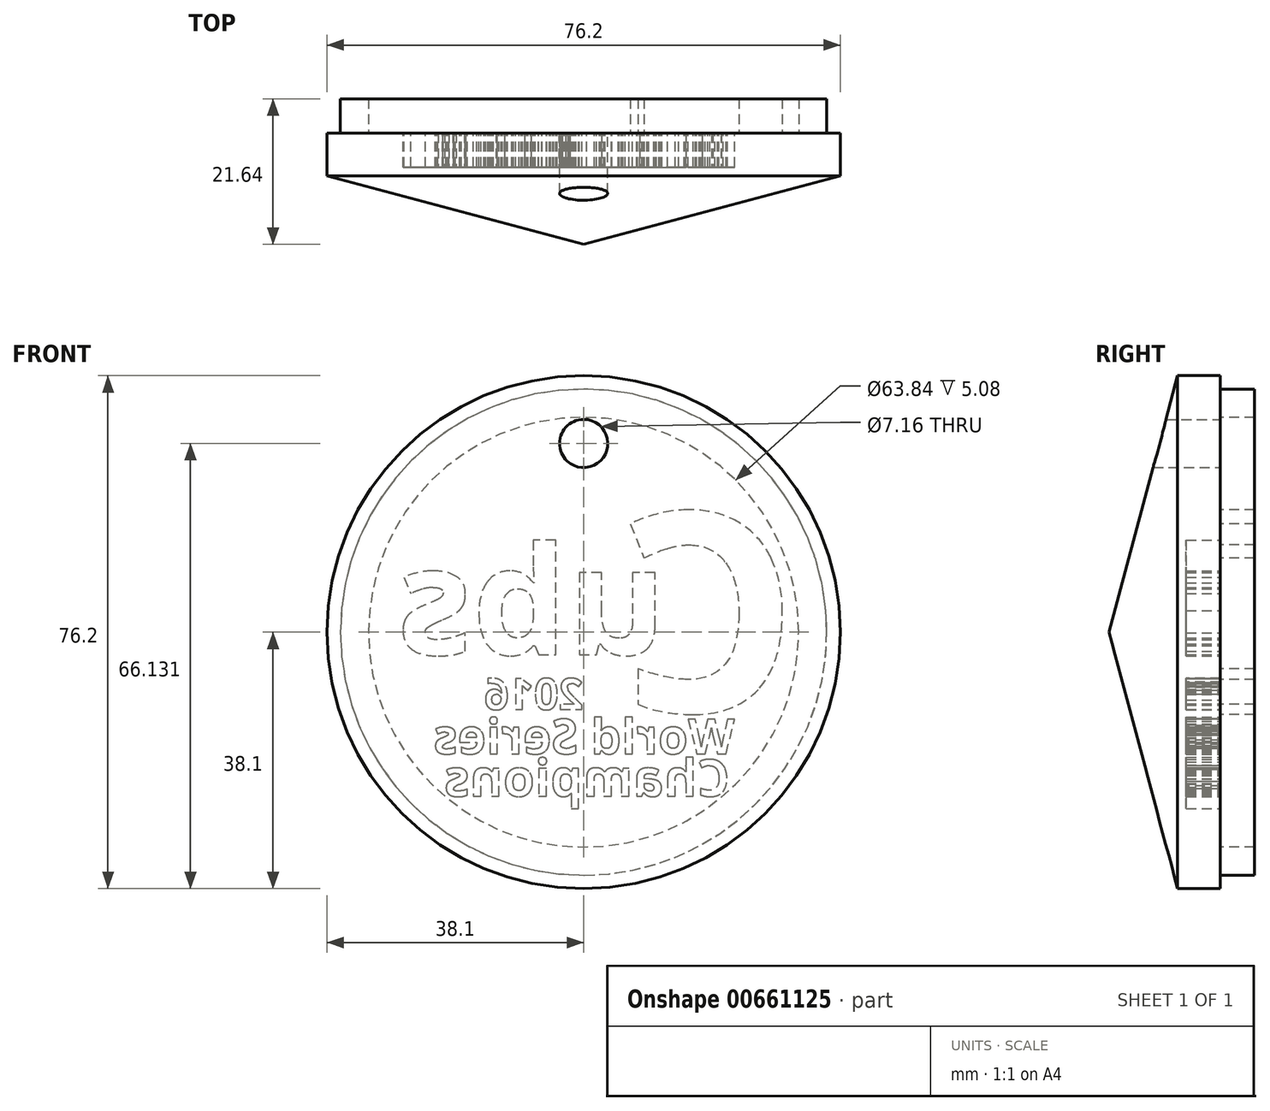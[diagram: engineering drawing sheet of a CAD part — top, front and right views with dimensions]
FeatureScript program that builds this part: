
annotation { "Feature Type Name" : "Feature", "Feature Type Description" : "" }
export const myFeature = defineFeature(function(context is Context, id is Id, definition is map)
    precondition{}
    {
        {
            var Q0;
            Q0=qCreatedBy(makeId("Front.planeOp"),FACE);
            var sketch = newSketch(context, id + "F0", { "sketchPlane" : qUnion([Q0])});
            skCircle(sketch, "E0", {"center": v(0, 0) * mm, "radius": 38.1 * mm});
            skSolve(sketch);
        }
        {
            var Q0;
            Q0=makeQuery(id+"F0.imprint","IMPRINT",FACE,{"disambiguationData":[TD([[makeQuery(id+"F0.imprint","IMPRINT",EDGE,{"derivedFrom":sQuery(id+"F0.wireOp",EDGE,"E0")}),1.0]])]});
            extrude(context, id + "F1", {"entities" : qUnion([Q0]), "oppositeDirection" : true, "depth" : 6.35 * mm, "offsetDistance" : 25.4 * mm});
        }
        {
            var Q0;
            Q0=makeQuery(id+"F1.opExtrude","CAP_FACE",FACE,{"disambiguationData":[OSD([sQuery(id+"F0.wireOp",EDGE,"E0")])],"isStart":false});
            var sketch = newSketch(context, id + "F2", { "sketchPlane" : qUnion([Q0])});
            skText(sketch, "E1", { "text": "C", "fontName": "OpenSans-Bold.ttf"});
            const initialGuessF2  = {"E1": [-0.0319, -0.01183, 1, 0, 0.02984]};
            skSetInitialGuess(sketch, initialGuessF2);
            skSolve(sketch);
        }
        {
            var Q0;
            Q0=makeQuery(id+"F2.imprint","IMPRINT",FACE,{"disambiguationData":[TD([[makeQuery(id+"F2.imprint","IMPRINT",EDGE,{"derivedFrom":sQuery(id+"F2.wireOp",EDGE,"E1.sketch_text.stroke-0")}),1.0]])]});
            var sketch = newSketch(context, id + "F3", { "sketchPlane" : qUnion([Q0])});
            skText(sketch, "E2", { "text": "ubs", "fontName": "OpenSans-Bold.ttf"});
            const initialGuessF3  = {"E2": [-0.01228, -0.00332, 1, 0, 0.01609]};
            skSetInitialGuess(sketch, initialGuessF3);
            skSolve(sketch);
        }
        {
            var Q0;
            Q0=makeQuery(id+"F3.imprint","IMPRINT",FACE,{"disambiguationData":[TD([[makeQuery(id+"F3.imprint","IMPRINT",EDGE,{"derivedFrom":sQuery(id+"F3.wireOp",EDGE,"E2.sketch_text.stroke-0")}),-1.0]])]});
            var Q1;
            Q1=makeQuery(id+"F3.imprint","IMPRINT",FACE,{"disambiguationData":[TD([[makeQuery(id+"F3.imprint","IMPRINT",EDGE,{"derivedFrom":sQuery(id+"F3.wireOp",EDGE,"E2.sketch_text.stroke-40")}),-1.0]])]});
            var Q2;
            Q2=makeQuery(id+"F3.imprint","IMPRINT",FACE,{"disambiguationData":[TD([[makeQuery(id+"F3.imprint","IMPRINT",EDGE,{"derivedFrom":sQuery(id+"F3.wireOp",EDGE,"E2.sketch_text.stroke-17")}),-1.0]])]});
            var Q3;
            Q3=makeQuery(id+"F1.opExtrude","CAP_FACE",FACE,{"disambiguationData":[OSD([sQuery(id+"F0.wireOp",EDGE,"E0")])],"isStart":true});
            extrude(context, id + "F4", {"entities" : qUnion([Q0, Q1, Q2, Q3]), "operationType" : NewBodyOperationType.REMOVE, "oppositeDirection" : true, "depth" : 5.08 * mm, "offsetDistance" : 25.4 * mm});
        }
        {
            var Q0;
            Q0=makeQuery(id+"F1.opExtrude","CAP_FACE",FACE,{"disambiguationData":[OSD([sQuery(id+"F0.wireOp",EDGE,"E0")])],"isStart":true});
            extrude(context, id + "F5", {"entities" : qUnion([Q0]), "operationType" : NewBodyOperationType.ADD, "depth" : 25.4 * mm, "offsetDistance" : 25.4 * mm, "hasDraft" : true, "draftAngle" : 75 * degree, "draftPullDirection" : true});
        }
        {
            var Q0;
            {var subQ0=sQuery(id+"F0.wireOp",EDGE,"E0");Q0=makeQuery(id+"F4.boolean.opBoolean","SPLIT",FACE,{"disambiguationData":[TD([makeQuery(id+"F1.opExtrude","SWEPT_FACE",FACE,{"disambiguationData":[OSD([subQ0])]})])],"derivedFrom":makeQuery(id+"F1.opExtrude","CAP_FACE",FACE,{"disambiguationData":[OSD([subQ0])],"isStart":false})});}
            var sketch = newSketch(context, id + "F6", { "sketchPlane" : qUnion([Q0])});
            skCircle(sketch, "E3", {"center": v(0, 28.03) * mm, "radius": 3.58 * mm});
            skSolve(sketch);
        }
        {
            var Q0;
            Q0=makeQuery(id+"F6.imprint","IMPRINT",FACE,{"disambiguationData":[TD([[makeQuery(id+"F6.imprint","IMPRINT",EDGE,{"derivedFrom":sQuery(id+"F6.wireOp",EDGE,"E3")}),1.0]])]});
            extrude(context, id + "F7", {"entities" : qUnion([Q0]), "operationType" : NewBodyOperationType.REMOVE, "oppositeDirection" : true, "depth" : 25.4 * mm, "offsetDistance" : 25.4 * mm});
        }
        {
            var Q0;
            Q0=makeQuery(id+"F4.boolean.opBoolean","COPY",FACE,{"derivedFrom":makeQuery(id+"F4.opExtrude","CAP_FACE",FACE,{"disambiguationData":[OSD([sQuery(id+"F3.wireOp",EDGE,"E2.sketch_text.stroke-0"),sQuery(id+"F3.wireOp",EDGE,"E2.sketch_text.stroke-1"),sQuery(id+"F3.wireOp",EDGE,"E2.sketch_text.stroke-2"),sQuery(id+"F3.wireOp",EDGE,"E2.sketch_text.stroke-3"),sQuery(id+"F3.wireOp",EDGE,"E2.sketch_text.stroke-4"),sQuery(id+"F3.wireOp",EDGE,"E2.sketch_text.stroke-5"),sQuery(id+"F3.wireOp",EDGE,"E2.sketch_text.stroke-6"),sQuery(id+"F3.wireOp",EDGE,"E2.sketch_text.stroke-7"),sQuery(id+"F3.wireOp",EDGE,"E2.sketch_text.stroke-8"),sQuery(id+"F3.wireOp",EDGE,"E2.sketch_text.stroke-9"),sQuery(id+"F3.wireOp",EDGE,"E2.sketch_text.stroke-10"),sQuery(id+"F3.wireOp",EDGE,"E2.sketch_text.stroke-11"),sQuery(id+"F3.wireOp",EDGE,"E2.sketch_text.stroke-12"),sQuery(id+"F3.wireOp",EDGE,"E2.sketch_text.stroke-13"),sQuery(id+"F3.wireOp",EDGE,"E2.sketch_text.stroke-14"),sQuery(id+"F3.wireOp",EDGE,"E2.sketch_text.stroke-15"),sQuery(id+"F3.wireOp",EDGE,"E2.sketch_text.stroke-16")])],"isStart":false})});
            var Q1;
            Q1=makeQuery(id+"F4.boolean.opBoolean","COPY",FACE,{"derivedFrom":makeQuery(id+"F4.opExtrude","CAP_FACE",FACE,{"disambiguationData":[OSD([sQuery(id+"F3.wireOp",EDGE,"E2.sketch_text.stroke-17"),sQuery(id+"F3.wireOp",EDGE,"E2.sketch_text.stroke-18"),sQuery(id+"F3.wireOp",EDGE,"E2.sketch_text.stroke-19"),sQuery(id+"F3.wireOp",EDGE,"E2.sketch_text.stroke-20"),sQuery(id+"F3.wireOp",EDGE,"E2.sketch_text.stroke-21"),sQuery(id+"F3.wireOp",EDGE,"E2.sketch_text.stroke-22"),sQuery(id+"F3.wireOp",EDGE,"E2.sketch_text.stroke-23"),sQuery(id+"F3.wireOp",EDGE,"E2.sketch_text.stroke-24"),sQuery(id+"F3.wireOp",EDGE,"E2.sketch_text.stroke-25"),sQuery(id+"F3.wireOp",EDGE,"E2.sketch_text.stroke-26"),sQuery(id+"F3.wireOp",EDGE,"E2.sketch_text.stroke-27"),sQuery(id+"F3.wireOp",EDGE,"E2.sketch_text.stroke-28"),sQuery(id+"F3.wireOp",EDGE,"E2.sketch_text.stroke-29"),sQuery(id+"F3.wireOp",EDGE,"E2.sketch_text.stroke-30"),sQuery(id+"F3.wireOp",EDGE,"E2.sketch_text.stroke-31"),sQuery(id+"F3.wireOp",EDGE,"E2.sketch_text.stroke-32"),sQuery(id+"F3.wireOp",EDGE,"E2.sketch_text.stroke-33"),sQuery(id+"F3.wireOp",EDGE,"E2.sketch_text.stroke-34"),sQuery(id+"F3.wireOp",EDGE,"E2.sketch_text.stroke-35"),sQuery(id+"F3.wireOp",EDGE,"E2.sketch_text.stroke-36"),sQuery(id+"F3.wireOp",EDGE,"E2.sketch_text.stroke-37"),sQuery(id+"F3.wireOp",EDGE,"E2.sketch_text.stroke-38"),sQuery(id+"F3.wireOp",EDGE,"E2.sketch_text.stroke-39")])],"isStart":false})});
            var Q2;
            Q2=makeQuery(id+"F4.boolean.opBoolean","COPY",FACE,{"derivedFrom":makeQuery(id+"F4.opExtrude","CAP_FACE",FACE,{"disambiguationData":[OSD([sQuery(id+"F3.wireOp",EDGE,"E2.sketch_text.stroke-40"),sQuery(id+"F3.wireOp",EDGE,"E2.sketch_text.stroke-41"),sQuery(id+"F3.wireOp",EDGE,"E2.sketch_text.stroke-42"),sQuery(id+"F3.wireOp",EDGE,"E2.sketch_text.stroke-43"),sQuery(id+"F3.wireOp",EDGE,"E2.sketch_text.stroke-44"),sQuery(id+"F3.wireOp",EDGE,"E2.sketch_text.stroke-45"),sQuery(id+"F3.wireOp",EDGE,"E2.sketch_text.stroke-46"),sQuery(id+"F3.wireOp",EDGE,"E2.sketch_text.stroke-47"),sQuery(id+"F3.wireOp",EDGE,"E2.sketch_text.stroke-48"),sQuery(id+"F3.wireOp",EDGE,"E2.sketch_text.stroke-49"),sQuery(id+"F3.wireOp",EDGE,"E2.sketch_text.stroke-50"),sQuery(id+"F3.wireOp",EDGE,"E2.sketch_text.stroke-51"),sQuery(id+"F3.wireOp",EDGE,"E2.sketch_text.stroke-52"),sQuery(id+"F3.wireOp",EDGE,"E2.sketch_text.stroke-53"),sQuery(id+"F3.wireOp",EDGE,"E2.sketch_text.stroke-54"),sQuery(id+"F3.wireOp",EDGE,"E2.sketch_text.stroke-55"),sQuery(id+"F3.wireOp",EDGE,"E2.sketch_text.stroke-56"),sQuery(id+"F3.wireOp",EDGE,"E2.sketch_text.stroke-57"),sQuery(id+"F3.wireOp",EDGE,"E2.sketch_text.stroke-58"),sQuery(id+"F3.wireOp",EDGE,"E2.sketch_text.stroke-59"),sQuery(id+"F3.wireOp",EDGE,"E2.sketch_text.stroke-60"),sQuery(id+"F3.wireOp",EDGE,"E2.sketch_text.stroke-61"),sQuery(id+"F3.wireOp",EDGE,"E2.sketch_text.stroke-62"),sQuery(id+"F3.wireOp",EDGE,"E2.sketch_text.stroke-63"),sQuery(id+"F3.wireOp",EDGE,"E2.sketch_text.stroke-64"),sQuery(id+"F3.wireOp",EDGE,"E2.sketch_text.stroke-65")])],"isStart":false})});
            extrude(context, id + "F8", {"entities" : qUnion([Q0, Q1, Q2]), "operationType" : NewBodyOperationType.REMOVE, "depth" : 5.08 * mm, "offsetDistance" : 25.4 * mm});
        }
        {
            var Q0;
            Q0=makeQuery(id+"F6.imprint","IMPRINT",FACE,{"disambiguationData":[TD([[makeQuery(id+"F6.imprint","IMPRINT",EDGE,{"derivedFrom":sQuery(id+"F6.wireOp",EDGE,"E3")}),-1.0]])]});
            var sketch = newSketch(context, id + "F9", { "sketchPlane" : qUnion([Q0])});
            skCircle(sketch, "E4", {"center": v(0, 0) * mm, "radius": 31.92 * mm});
            skCircle(sketch, "E5", {"center": v(0, 0) * mm, "radius": 36.1 * mm});
            skSolve(sketch);
        }
        {
            var Q0;
            Q0=makeQuery(id+"F9.imprint","IMPRINT",FACE,{"disambiguationData":[TD([[makeQuery(id+"F9.imprint","IMPRINT",EDGE,{"derivedFrom":sQuery(id+"F9.wireOp",EDGE,"E4")}),-1.0]])]});
            extrude(context, id + "F10", {"entities" : qUnion([Q0]), "operationType" : NewBodyOperationType.ADD, "depth" : 5.08 * mm, "offsetDistance" : 25.4 * mm});
        }
        {
            var Q0;
            Q0 = qSketchRegion(id + "F2", true);
            extrude(context, id + "F11", {"entities" : qUnion([Q0]), "operationType" : NewBodyOperationType.ADD, "depth" : 5.08 * mm, "offsetDistance" : 25.4 * mm});
        }
        {
            var Q0;
            Q0=makeQuery(id+"F6.imprint","IMPRINT",FACE,{"disambiguationData":[TD([[makeQuery(id+"F6.imprint","IMPRINT",EDGE,{"derivedFrom":sQuery(id+"F6.wireOp",EDGE,"E3")}),-1.0]])]});
            var sketch = newSketch(context, id + "F12", { "sketchPlane" : qUnion([Q0])});
            skText(sketch, "E6", { "text": "2016\n", "fontName": "OpenSans-Bold.ttf"});
            skText(sketch, "E7", { "text": "World Series", "fontName": "OpenSans-Bold.ttf"});
            const initialGuessF12  = {"E6": [0, -0.0115, 1, 0, 0.00466], "E7": [-0.02243, -0.01806, 1, 0, 0.00517]};
            skSetInitialGuess(sketch, initialGuessF12);
            skSolve(sketch);
        }
        {
            var Q0;
            Q0=makeQuery(id+"F12.imprint","IMPRINT",FACE,{"disambiguationData":[TD([[makeQuery(id+"F12.imprint","IMPRINT",EDGE,{"derivedFrom":sQuery(id+"F12.wireOp",EDGE,"E6.sketch_text.stroke-0")}),1.0]])]});
            var sketch = newSketch(context, id + "F13", { "sketchPlane" : qUnion([Q0])});
            skText(sketch, "E8", { "text": "Champions", "fontName": "OpenSans-Bold.ttf"});
            const initialGuessF13  = {"E8": [-0.0217, -0.02436, 1, 0, 0.00546]};
            skSetInitialGuess(sketch, initialGuessF13);
            skSolve(sketch);
        }
        {
            var Q0;
            Q0 = qSketchRegion(id + "F12", true);
            extrude(context, id + "F14", {"entities" : qUnion([Q0]), "operationType" : NewBodyOperationType.REMOVE, "oppositeDirection" : true, "depth" : 5.08 * mm, "offsetDistance" : 25.4 * mm});
        }
        {
            var Q0;
            Q0 = qSketchRegion(id + "F13", true);
            extrude(context, id + "F15", {"entities" : qUnion([Q0]), "operationType" : NewBodyOperationType.REMOVE, "oppositeDirection" : true, "depth" : 5.08 * mm, "offsetDistance" : 25.4 * mm});
        }
    });
